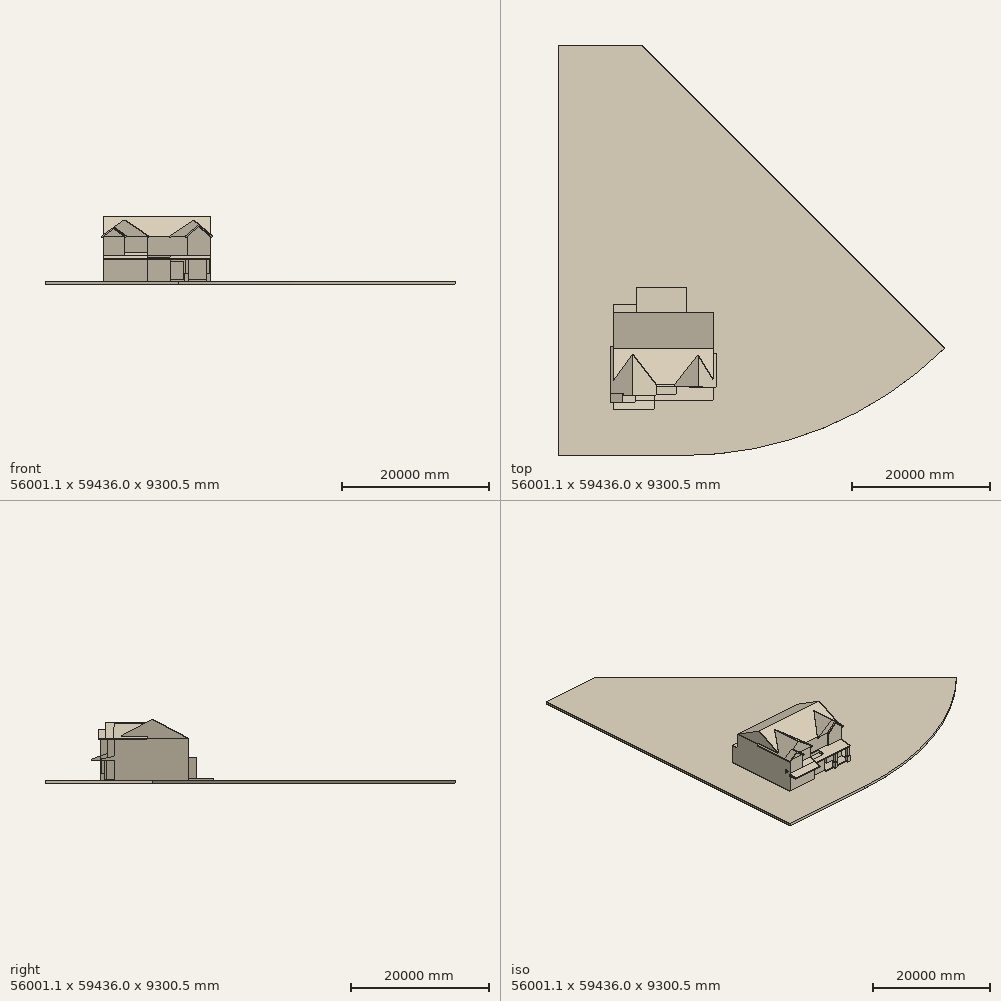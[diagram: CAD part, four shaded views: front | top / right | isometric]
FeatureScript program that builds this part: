
annotation { "Feature Type Name" : "Feature", "Feature Type Description" : "" }
export const myFeature = defineFeature(function(context is Context, id is Id, definition is map)
    precondition{}
    {
        {
            var Q0;
            Q0=qCreatedBy(makeId("Top.planeOp"),FACE);
            var sketch = newSketch(context, id + "F0", { "sketchPlane" : qUnion([Q0])});
            skLineSegment(sketch, "E0", {"start": v(-9470.01, 30042.55) * mm, "end": v(2593.97, 30042.55) * mm});
            skLineSegment(sketch, "E1", {"start": v(8689.97, -29393.45) * mm, "end": v(-9470.01, -29393.45) * mm});
            skLineSegment(sketch, "E2", {"start": v(-9470.01, -29393.45) * mm, "end": v(-9470.01, 30042.55) * mm});
            skLineSegment(sketch, "E3", {"start": v(2593.97, 30042.55) * mm, "end": v(46531.13, -13894.61) * mm});
            skArc(sketch, "E4", {"start": v(8689.97, -29393.45) * mm, "mid": v(29136.04, -25368.6) * mm, "end": v(46531.13, -13894.61) * mm});
            skSolve(sketch);
        }
        {
            var Q0;
            Q0=makeQuery(id+"F0.imprint","IMPRINT",FACE,{"disambiguationData":[TD([[makeQuery(id+"F0.imprint","IMPRINT",EDGE,{"derivedFrom":sQuery(id+"F0.wireOp",EDGE,"E0")}),-1.0]])]});
            extrude(context, id + "F1", {"entities" : qUnion([Q0]), "depth" : 457.2 * mm, "offsetDistance" : 25.4 * mm});
        }
        {
            var Q0;
            Q0=makeQuery(id+"F1.opExtrude","CAP_FACE",FACE,{"disambiguationData":[OSD([sQuery(id+"F0.wireOp",EDGE,"E0"),sQuery(id+"F0.wireOp",EDGE,"E1"),sQuery(id+"F0.wireOp",EDGE,"E2"),sQuery(id+"F0.wireOp",EDGE,"E3"),sQuery(id+"F0.wireOp",EDGE,"E4")])],"isStart":false});
            var sketch = newSketch(context, id + "F2", { "sketchPlane" : qUnion([Q0])});
            skLineSegment(sketch, "E5.bottom", {"start": v(-1545.21, -21468.65) * mm, "end": v(13085.19, -21468.65) * mm});
            skLineSegment(sketch, "E5.top", {"start": v(-1545.21, -8667.05) * mm, "end": v(13085.19, -8667.05) * mm});
            skLineSegment(sketch, "E5.left", {"start": v(-1545.21, -21468.65) * mm, "end": v(-1545.21, -8667.05) * mm});
            skLineSegment(sketch, "E5.right", {"start": v(13085.19, -21468.65) * mm, "end": v(13085.19, -8667.05) * mm});
            skSolve(sketch);
        }
        {
            var Q0;
            Q0 = qSketchRegion(id + "F2", true);
            extrude(context, id + "F3", {"entities" : qUnion([Q0]), "operationType" : NewBodyOperationType.ADD, "depth" : 6096 * mm, "offsetDistance" : 25.4 * mm});
        }
        {
            var Q0;
            Q0=makeQuery(id+"F2.imprint","IMPRINT",FACE,{"disambiguationData":[TD([[makeQuery(id+"F2.imprint","IMPRINT",EDGE,{"derivedFrom":sQuery(id+"F2.wireOp",EDGE,"E5.bottom")}),-1.0]])]});
            var sketch = newSketch(context, id + "F4", { "sketchPlane" : qUnion([Q0])});
            skLineSegment(sketch, "E6.bottom", {"start": v(-1545.21, -7447.85) * mm, "end": v(1807.59, -7447.85) * mm});
            skLineSegment(sketch, "E6.top", {"start": v(-1545.21, -8667.05) * mm, "end": v(1807.59, -8667.05) * mm});
            skLineSegment(sketch, "E6.left", {"start": v(-1545.21, -7447.85) * mm, "end": v(-1545.21, -8667.05) * mm});
            skLineSegment(sketch, "E6.right", {"start": v(1807.59, -7447.85) * mm, "end": v(1807.59, -8667.05) * mm});
            skSolve(sketch);
        }
        {
            var Q0;
            Q0 = qSketchRegion(id + "F4", true);
            extrude(context, id + "F5", {"entities" : qUnion([Q0]), "operationType" : NewBodyOperationType.ADD, "depth" : 3352.8 * mm, "offsetDistance" : 25.4 * mm});
        }
        {
            var Q0;
            Q0=makeQuery(id+"F2.imprint","IMPRINT",FACE,{"disambiguationData":[TD([[makeQuery(id+"F2.imprint","IMPRINT",EDGE,{"derivedFrom":sQuery(id+"F2.wireOp",EDGE,"E5.bottom")}),-1.0]])]});
            var sketch = newSketch(context, id + "F6", { "sketchPlane" : qUnion([Q0])});
            skLineSegment(sketch, "E7.bottom", {"start": v(1807.59, -5009.45) * mm, "end": v(9122.79, -5009.45) * mm});
            skLineSegment(sketch, "E7.top", {"start": v(1807.59, -8667.05) * mm, "end": v(9122.79, -8667.05) * mm});
            skLineSegment(sketch, "E7.left", {"start": v(1807.59, -5009.45) * mm, "end": v(1807.59, -8667.05) * mm});
            skLineSegment(sketch, "E7.right", {"start": v(9122.79, -5009.45) * mm, "end": v(9122.79, -8667.05) * mm});
            skSolve(sketch);
        }
        {
            var Q0;
            Q0 = qSketchRegion(id + "F6", true);
            extrude(context, id + "F7", {"entities" : qUnion([Q0]), "operationType" : NewBodyOperationType.ADD, "depth" : 304.8 * mm, "offsetDistance" : 25.4 * mm});
        }
        {
            var Q0;
            Q0=makeQuery(id+"F3.opExtrude","SWEPT_FACE",FACE,{"disambiguationData":[OSD([sQuery(id+"F2.wireOp",EDGE,"E5.bottom")])]});
            var sketch = newSketch(context, id + "F8", { "sketchPlane" : qUnion([Q0])});
            skLineSegment(sketch, "E8.bottom", {"start": v(13085.19, 457.2) * mm, "end": v(7598.79, 457.2) * mm});
            skLineSegment(sketch, "E8.top", {"start": v(13085.19, 6553.2) * mm, "end": v(7598.79, 6553.2) * mm});
            skLineSegment(sketch, "E8.left", {"start": v(13085.19, 457.2) * mm, "end": v(13085.19, 6553.2) * mm});
            skLineSegment(sketch, "E8.right", {"start": v(7598.79, 457.2) * mm, "end": v(7598.79, 6553.2) * mm});
            skSolve(sketch);
        }
        {
            var Q0;
            Q0 = qSketchRegion(id + "F8", true);
            extrude(context, id + "F9", {"entities" : qUnion([Q0]), "operationType" : NewBodyOperationType.REMOVE, "oppositeDirection" : true, "depth" : 2133.6 * mm, "offsetDistance" : 25.4 * mm});
        }
        {
            var Q0;
            Q0=makeQuery(id+"F3.opExtrude","SWEPT_FACE",FACE,{"disambiguationData":[OSD([sQuery(id+"F2.wireOp",EDGE,"E5.bottom")])]});
            var sketch = newSketch(context, id + "F10", { "sketchPlane" : qUnion([Q0])});
            skLineSegment(sketch, "E9.bottom", {"start": v(7598.79, 6553.2) * mm, "end": v(4398.39, 6553.2) * mm});
            skLineSegment(sketch, "E9.top", {"start": v(7598.79, 457.2) * mm, "end": v(4398.39, 457.2) * mm});
            skLineSegment(sketch, "E9.left", {"start": v(7598.79, 6553.2) * mm, "end": v(7598.79, 457.2) * mm});
            skLineSegment(sketch, "E9.right", {"start": v(4398.39, 6553.2) * mm, "end": v(4398.39, 457.2) * mm});
            skSolve(sketch);
        }
        {
            var Q0;
            Q0 = qSketchRegion(id + "F10", true);
            extrude(context, id + "F11", {"entities" : qUnion([Q0]), "operationType" : NewBodyOperationType.REMOVE, "oppositeDirection" : true, "depth" : 914.4 * mm, "offsetDistance" : 25.4 * mm});
        }
        {
            var Q0;
            Q0=makeQuery(id+"F9.boolean.opBoolean","COPY",FACE,{"derivedFrom":makeQuery(id+"F9.opExtrude","CAP_FACE",FACE,{"disambiguationData":[OSD([sQuery(id+"F8.wireOp",EDGE,"E8.bottom"),sQuery(id+"F8.wireOp",EDGE,"E8.top"),sQuery(id+"F8.wireOp",EDGE,"E8.left"),sQuery(id+"F8.wireOp",EDGE,"E8.right")])],"isStart":false})});
            var sketch = newSketch(context, id + "F12", { "sketchPlane" : qUnion([Q0])});
            skLineSegment(sketch, "E10.bottom", {"start": v(7598.79, 457.2) * mm, "end": v(9427.59, 457.2) * mm});
            skLineSegment(sketch, "E10.top", {"start": v(7598.79, 3200.4) * mm, "end": v(9427.59, 3200.4) * mm});
            skLineSegment(sketch, "E10.left", {"start": v(7598.79, 457.2) * mm, "end": v(7598.79, 3200.4) * mm});
            skLineSegment(sketch, "E10.right", {"start": v(9427.59, 457.2) * mm, "end": v(9427.59, 3200.4) * mm});
            skSolve(sketch);
        }
        {
            var Q0;
            Q0 = qSketchRegion(id + "F12", true);
            extrude(context, id + "F13", {"entities" : qUnion([Q0]), "operationType" : NewBodyOperationType.REMOVE, "oppositeDirection" : true, "depth" : 457.2 * mm, "offsetDistance" : 25.4 * mm});
        }
        {
            var Q0;
            Q0=makeQuery(id+"F3.opExtrude","SWEPT_FACE",FACE,{"disambiguationData":[OSD([sQuery(id+"F2.wireOp",EDGE,"E5.right")])]});
            var sketch = newSketch(context, id + "F14", { "sketchPlane" : qUnion([Q0])});
            skLineSegment(sketch, "E11", {"start": v(-19335.05, 3352.8) * mm, "end": v(-21417.85, 3352.8) * mm});
            skLineSegment(sketch, "E12", {"start": v(-21417.85, 3352.8) * mm, "end": v(-21417.85, 3505.2) * mm});
            skLineSegment(sketch, "E13", {"start": v(-21417.85, 3505.2) * mm, "end": v(-19335.05, 3962.4) * mm});
            skLineSegment(sketch, "E14", {"start": v(-19335.05, 3962.4) * mm, "end": v(-19335.05, 3352.8) * mm});
            skSolve(sketch);
        }
        {
            var Q0;
            Q0 = qSketchRegion(id + "F14", true);
            extrude(context, id + "F15", {"entities" : qUnion([Q0]), "oppositeDirection" : true, "depth" : 8839.2 * mm, "offsetDistance" : 25.4 * mm});
        }
        {
            var Q0;
            Q0=makeQuery(id+"F5.boolean.opBoolean","MERGE",FACE,{"derivedFrom":[makeQuery(id+"F3.opExtrude","SWEPT_FACE",FACE,{"disambiguationData":[OSD([sQuery(id+"F2.wireOp",EDGE,"E5.left")])]}),makeQuery(id+"F5.opExtrude","SWEPT_FACE",FACE,{"disambiguationData":[OSD([sQuery(id+"F4.wireOp",EDGE,"E6.left")])]})]});
            var sketch = newSketch(context, id + "F16", { "sketchPlane" : qUnion([Q0])});
            skLineSegment(sketch, "E15", {"start": v(21468.65, 3352.8) * mm, "end": v(22789.45, 3352.8) * mm});
            skLineSegment(sketch, "E16", {"start": v(22789.45, 3352.8) * mm, "end": v(22789.45, 3505.2) * mm});
            skLineSegment(sketch, "E17", {"start": v(22789.45, 3505.2) * mm, "end": v(21468.65, 3962.4) * mm});
            skLineSegment(sketch, "E18", {"start": v(21468.65, 3962.4) * mm, "end": v(21468.65, 3352.8) * mm});
            skSolve(sketch);
        }
        {
            var Q0;
            Q0 = qSketchRegion(id + "F16", true);
            extrude(context, id + "F17", {"entities" : qUnion([Q0]), "operationType" : NewBodyOperationType.ADD, "oppositeDirection" : true, "depth" : 5943.6 * mm, "offsetDistance" : 25.4 * mm});
        }
        {
            var Q0;
            Q0=makeQuery(id+"F15.opExtrude","SWEPT_FACE",FACE,{"disambiguationData":[OSD([sQuery(id+"F14.wireOp",EDGE,"E11")])]});
            var sketch = newSketch(context, id + "F18", { "sketchPlane" : qUnion([Q0])});
            skLineSegment(sketch, "E19.bottom", {"start": v(13085.19, 21417.85) * mm, "end": v(12475.59, 21417.85) * mm});
            skLineSegment(sketch, "E19.top", {"start": v(13085.19, 20808.25) * mm, "end": v(12475.59, 20808.25) * mm});
            skLineSegment(sketch, "E19.left", {"start": v(13085.19, 21417.85) * mm, "end": v(13085.19, 20808.25) * mm});
            skLineSegment(sketch, "E19.right", {"start": v(12475.59, 21417.85) * mm, "end": v(12475.59, 20808.25) * mm});
            skLineSegment(sketch, "E20.bottom", {"start": v(9511.45, 21417.85) * mm, "end": v(10121.05, 21417.85) * mm});
            skLineSegment(sketch, "E20.top", {"start": v(9511.45, 20808.25) * mm, "end": v(10121.05, 20808.25) * mm});
            skLineSegment(sketch, "E20.left", {"start": v(9511.45, 21417.85) * mm, "end": v(9511.45, 20808.25) * mm});
            skLineSegment(sketch, "E20.right", {"start": v(10121.05, 21417.85) * mm, "end": v(10121.05, 20808.25) * mm});
            skSolve(sketch);
        }
        {
            var Q0;
            Q0 = qSketchRegion(id + "F18", true);
            extrude(context, id + "F19", {"entities" : qUnion([Q0]), "depth" : 3048 * mm, "offsetDistance" : 25.4 * mm});
        }
        {
            var Q0;
            Q0=makeQuery(id+"F13.boolean.opBoolean","MERGE",FACE,{"derivedFrom":[makeQuery(id+"F11.boolean.opBoolean","MERGE",FACE,{"derivedFrom":[makeQuery(id+"F9.boolean.opBoolean","MERGE",FACE,{"derivedFrom":[makeQuery(id+"F1.opExtrude","CAP_FACE",FACE,{"disambiguationData":[OSD([sQuery(id+"F0.wireOp",EDGE,"E0"),sQuery(id+"F0.wireOp",EDGE,"E1"),sQuery(id+"F0.wireOp",EDGE,"E2"),sQuery(id+"F0.wireOp",EDGE,"E3"),sQuery(id+"F0.wireOp",EDGE,"E4")])],"isStart":false})],"fromTools":[makeQuery(id+"F9.opExtrude","SWEPT_FACE",FACE,{"disambiguationData":[OSD([sQuery(id+"F8.wireOp",EDGE,"E8.bottom")])]})]})],"fromTools":[makeQuery(id+"F11.opExtrude","SWEPT_FACE",FACE,{"disambiguationData":[OSD([sQuery(id+"F10.wireOp",EDGE,"E9.top")])]})]})],"fromTools":[makeQuery(id+"F13.opExtrude","SWEPT_FACE",FACE,{"disambiguationData":[OSD([sQuery(id+"F12.wireOp",EDGE,"E10.bottom")])]})]});
            var sketch = newSketch(context, id + "F20", { "sketchPlane" : qUnion([Q0])});
            skLineSegment(sketch, "E21.bottom", {"start": v(7598.79, -18877.85) * mm, "end": v(13078.42, -18877.85) * mm});
            skLineSegment(sketch, "E21.top", {"start": v(7598.79, -21050.32) * mm, "end": v(13078.42, -21050.32) * mm});
            skLineSegment(sketch, "E21.left", {"start": v(7598.79, -18877.85) * mm, "end": v(7598.79, -21050.32) * mm});
            skLineSegment(sketch, "E21.right", {"start": v(13078.42, -18877.85) * mm, "end": v(13078.42, -21050.32) * mm});
            skSolve(sketch);
        }
        {
            var Q0;
            Q0 = qSketchRegion(id + "F20", true);
            extrude(context, id + "F21", {"entities" : qUnion([Q0]), "depth" : 203.2 * mm, "offsetDistance" : 25.4 * mm});
        }
        {
            var Q0;
            Q0=makeQuery(id+"F15.opExtrude","SWEPT_FACE",FACE,{"disambiguationData":[OSD([sQuery(id+"F14.wireOp",EDGE,"E11")])]});
            var sketch = newSketch(context, id + "F22", { "sketchPlane" : qUnion([Q0])});
            skLineSegment(sketch, "E22.bottom", {"start": v(13085.19, 21417.85) * mm, "end": v(12475.59, 21417.85) * mm});
            skLineSegment(sketch, "E22.top", {"start": v(13085.19, 20808.25) * mm, "end": v(12475.59, 20808.25) * mm});
            skLineSegment(sketch, "E22.left", {"start": v(13085.19, 21417.85) * mm, "end": v(13085.19, 20808.25) * mm});
            skLineSegment(sketch, "E22.right", {"start": v(12475.59, 21417.85) * mm, "end": v(12475.59, 20808.25) * mm});
            skLineSegment(sketch, "E23.bottom", {"start": v(10122.32, 21417.85) * mm, "end": v(9487.32, 21417.85) * mm});
            skLineSegment(sketch, "E23.top", {"start": v(10122.32, 20808.25) * mm, "end": v(9487.32, 20808.25) * mm});
            skLineSegment(sketch, "E23.left", {"start": v(10122.32, 21417.85) * mm, "end": v(10122.32, 20808.25) * mm});
            skLineSegment(sketch, "E23.right", {"start": v(9487.32, 21417.85) * mm, "end": v(9487.32, 20808.25) * mm});
            skLineSegment(sketch, "E24.bottom", {"start": v(10020.72, 21316.25) * mm, "end": v(9614.32, 21316.25) * mm});
            skLineSegment(sketch, "E24.top", {"start": v(10020.72, 20909.85) * mm, "end": v(9614.32, 20909.85) * mm});
            skLineSegment(sketch, "E24.left", {"start": v(10020.72, 21316.25) * mm, "end": v(10020.72, 20909.85) * mm});
            skLineSegment(sketch, "E24.right", {"start": v(9614.32, 21316.25) * mm, "end": v(9614.32, 20909.85) * mm});
            skLineSegment(sketch, "E25.bottom", {"start": v(12577.19, 20909.85) * mm, "end": v(12983.59, 20909.85) * mm});
            skLineSegment(sketch, "E25.top", {"start": v(12577.19, 21316.25) * mm, "end": v(12983.59, 21316.25) * mm});
            skLineSegment(sketch, "E25.left", {"start": v(12577.19, 20909.85) * mm, "end": v(12577.19, 21316.25) * mm});
            skLineSegment(sketch, "E25.right", {"start": v(12983.59, 20909.85) * mm, "end": v(12983.59, 21316.25) * mm});
            skSolve(sketch);
        }
        {
            var Q0;
            Q0 = qSketchRegion(id + "F22", true);
            extrude(context, id + "F23", {"entities" : qUnion([Q0]), "operationType" : NewBodyOperationType.REMOVE, "depth" : 1828.8 * mm, "offsetDistance" : 25.4 * mm});
        }
        {
            var Q0;
            Q0=makeQuery(id+"F11.boolean.opBoolean","COPY",FACE,{"derivedFrom":makeQuery(id+"F11.opExtrude","CAP_FACE",FACE,{"disambiguationData":[OSD([sQuery(id+"F10.wireOp",EDGE,"E9.bottom"),sQuery(id+"F10.wireOp",EDGE,"E9.top"),sQuery(id+"F10.wireOp",EDGE,"E9.left"),sQuery(id+"F10.wireOp",EDGE,"E9.right")])],"isStart":false})});
            var sketch = newSketch(context, id + "F24", { "sketchPlane" : qUnion([Q0])});
            skLineSegment(sketch, "E26.bottom", {"start": v(4398.39, 6553.2) * mm, "end": v(7598.79, 6553.2) * mm});
            skLineSegment(sketch, "E26.top", {"start": v(4398.39, 3505.2) * mm, "end": v(7598.79, 3505.2) * mm});
            skLineSegment(sketch, "E26.left", {"start": v(4398.39, 6553.2) * mm, "end": v(4398.39, 3505.2) * mm});
            skLineSegment(sketch, "E26.right", {"start": v(7598.79, 6553.2) * mm, "end": v(7598.79, 3505.2) * mm});
            skSolve(sketch);
        }
        {
            var Q0;
            Q0 = qSketchRegion(id + "F24", true);
            extrude(context, id + "F25", {"entities" : qUnion([Q0]), "operationType" : NewBodyOperationType.REMOVE, "oppositeDirection" : true, "depth" : 1219.2 * mm, "offsetDistance" : 25.4 * mm});
        }
        {
            var Q0;
            Q0=makeQuery(id+"F25.boolean.opBoolean","MERGE",FACE,{"derivedFrom":[makeQuery(id+"F9.boolean.opBoolean","COPY",FACE,{"derivedFrom":makeQuery(id+"F9.opExtrude","CAP_FACE",FACE,{"disambiguationData":[OSD([sQuery(id+"F8.wireOp",EDGE,"E8.bottom"),sQuery(id+"F8.wireOp",EDGE,"E8.top"),sQuery(id+"F8.wireOp",EDGE,"E8.left"),sQuery(id+"F8.wireOp",EDGE,"E8.right")])],"isStart":false})})],"fromTools":[makeQuery(id+"F25.opExtrude","CAP_FACE",FACE,{"disambiguationData":[OSD([sQuery(id+"F24.wireOp",EDGE,"E26.bottom"),sQuery(id+"F24.wireOp",EDGE,"E26.top"),sQuery(id+"F24.wireOp",EDGE,"E26.left"),sQuery(id+"F24.wireOp",EDGE,"E26.right")])],"isStart":false})]});
            var sketch = newSketch(context, id + "F26", { "sketchPlane" : qUnion([Q0])});
            skLineSegment(sketch, "E27.bottom", {"start": v(4398.39, 6553.2) * mm, "end": v(9914.34, 6553.2) * mm});
            skLineSegment(sketch, "E27.top", {"start": v(4398.39, 3962.4) * mm, "end": v(9914.34, 3962.4) * mm});
            skLineSegment(sketch, "E27.left", {"start": v(4398.39, 6553.2) * mm, "end": v(4398.39, 3962.4) * mm});
            skLineSegment(sketch, "E27.right", {"start": v(9914.34, 6553.2) * mm, "end": v(9914.34, 3962.4) * mm});
            skSolve(sketch);
        }
        {
            var Q0;
            Q0 = qSketchRegion(id + "F26", true);
            extrude(context, id + "F27", {"entities" : qUnion([Q0]), "operationType" : NewBodyOperationType.REMOVE, "oppositeDirection" : true, "depth" : 254 * mm, "offsetDistance" : 25.4 * mm});
        }
        {
            var Q0;
            {var subQ1=sQuery(id+"F2.wireOp",EDGE,"E5.bottom");var subQ2=sQuery(id+"F16.wireOp",EDGE,"E17");Q0=makeQuery(id+"F17.boolean.opBoolean","SPLIT",FACE,{"disambiguationData":[TD([makeQuery(id+"F17.opExtrude","SWEPT_FACE",FACE,{"disambiguationData":[OSD([subQ2])]})])],"derivedFrom":makeQuery(id+"F3.opExtrude","SWEPT_FACE",FACE,{"disambiguationData":[OSD([subQ1])]})});}
            var sketch = newSketch(context, id + "F28", { "sketchPlane" : qUnion([Q0])});
            skLineSegment(sketch, "E28.bottom", {"start": v(4398.39, 6553.2) * mm, "end": v(1350.39, 6553.2) * mm});
            skLineSegment(sketch, "E28.top", {"start": v(4398.39, 3962.4) * mm, "end": v(1350.39, 3962.4) * mm});
            skLineSegment(sketch, "E28.left", {"start": v(4398.39, 6553.2) * mm, "end": v(4398.39, 3962.4) * mm});
            skLineSegment(sketch, "E28.right", {"start": v(1350.39, 6553.2) * mm, "end": v(1350.39, 3962.4) * mm});
            skSolve(sketch);
        }
        {
            var Q0;
            Q0 = qSketchRegion(id + "F28", true);
            extrude(context, id + "F29", {"entities" : qUnion([Q0]), "operationType" : NewBodyOperationType.REMOVE, "oppositeDirection" : true, "depth" : 1066.8 * mm, "offsetDistance" : 25.4 * mm});
        }
        {
            var Q0;
            {var subQ3=sQuery(id+"F16.wireOp",EDGE,"E18");Q0=makeQuery(id+"F16.imprint","IMPRINT",FACE,{"disambiguationData":[TD([[makeQuery(id+"F16.imprint","IMPRINT",EDGE,{"derivedFrom":subQ3}),-1.0]])]});}
            var sketch = newSketch(context, id + "F30", { "sketchPlane" : qUnion([Q0])});
            skLineSegment(sketch, "E29", {"start": v(21468.65, 3962.4) * mm, "end": v(21468.65, 3352.8) * mm});
            skLineSegment(sketch, "E30", {"start": v(21468.65, 3962.4) * mm, "end": v(20342.53, 4352.21) * mm});
            skLineSegment(sketch, "E31", {"start": v(20342.53, 4352.21) * mm, "end": v(20342.53, 3352.8) * mm});
            skLineSegment(sketch, "E32", {"start": v(20342.53, 3352.8) * mm, "end": v(21468.65, 3352.8) * mm});
            skSolve(sketch);
        }
        {
            var Q0;
            Q0 = qSketchRegion(id + "F30", true);
            extrude(context, id + "F31", {"entities" : qUnion([Q0]), "oppositeDirection" : true, "depth" : 5943.6 * mm, "offsetDistance" : 25.4 * mm});
        }
        {
            var Q0;
            {var subQ3=sQuery(id+"F14.wireOp",EDGE,"E14");Q0=makeQuery(id+"F14.imprint","IMPRINT",FACE,{"disambiguationData":[TD([[makeQuery(id+"F14.imprint","IMPRINT",EDGE,{"derivedFrom":subQ3}),1.0]])]});}
            var sketch = newSketch(context, id + "F32", { "sketchPlane" : qUnion([Q0])});
            skLineSegment(sketch, "E33", {"start": v(-19335.05, 3962.4) * mm, "end": v(-19335.05, 3352.8) * mm});
            skLineSegment(sketch, "E34", {"start": v(-19335.05, 3962.4) * mm, "end": v(-18821.67, 4075.1) * mm});
            skLineSegment(sketch, "E35", {"start": v(-18821.67, 4075.1) * mm, "end": v(-18821.67, 3352.8) * mm});
            skLineSegment(sketch, "E36", {"start": v(-18821.67, 3352.8) * mm, "end": v(-19335.05, 3352.8) * mm});
            skSolve(sketch);
        }
        {
            var Q0;
            Q0 = qSketchRegion(id + "F32", true);
            extrude(context, id + "F33", {"entities" : qUnion([Q0]), "operationType" : NewBodyOperationType.ADD, "oppositeDirection" : true, "depth" : 9144 * mm, "offsetDistance" : 25.4 * mm});
        }
        {
            var Q0;
            Q0=makeQuery(id+"F29.boolean.opBoolean","COPY",FACE,{"derivedFrom":makeQuery(id+"F29.opExtrude","CAP_FACE",FACE,{"disambiguationData":[OSD([sQuery(id+"F28.wireOp",EDGE,"E28.bottom"),sQuery(id+"F28.wireOp",EDGE,"E28.top"),sQuery(id+"F28.wireOp",EDGE,"E28.left"),sQuery(id+"F28.wireOp",EDGE,"E28.right")])],"isStart":false})});
            var sketch = newSketch(context, id + "F34", { "sketchPlane" : qUnion([Q0])});
            skLineSegment(sketch, "E37", {"start": v(1655.19, 6553.2) * mm, "end": v(-1850.01, 6553.2) * mm});
            skLineSegment(sketch, "E38", {"start": v(-1850.01, 6553.2) * mm, "end": v(-97.41, 7823.2) * mm});
            skLineSegment(sketch, "E39", {"start": v(-97.41, 7823.2) * mm, "end": v(1655.19, 6553.2) * mm});
            skLineSegment(sketch, "E40.bottom", {"start": v(1655.19, 6553.2) * mm, "end": v(1350.39, 6553.2) * mm});
            skLineSegment(sketch, "E40.top", {"start": v(1655.19, 6400.8) * mm, "end": v(1350.39, 6400.8) * mm});
            skLineSegment(sketch, "E40.left", {"start": v(1655.19, 6553.2) * mm, "end": v(1655.19, 6400.8) * mm});
            skLineSegment(sketch, "E40.right", {"start": v(1350.39, 6553.2) * mm, "end": v(1350.39, 6400.8) * mm});
            skLineSegment(sketch, "E41.bottom", {"start": v(-1850.01, 6553.2) * mm, "end": v(-1545.21, 6553.2) * mm});
            skLineSegment(sketch, "E41.top", {"start": v(-1850.01, 6400.8) * mm, "end": v(-1545.21, 6400.8) * mm});
            skLineSegment(sketch, "E41.left", {"start": v(-1850.01, 6553.2) * mm, "end": v(-1850.01, 6400.8) * mm});
            skLineSegment(sketch, "E41.right", {"start": v(-1545.21, 6553.2) * mm, "end": v(-1545.21, 6400.8) * mm});
            skSolve(sketch);
        }
        {
            var Q0;
            Q0 = qSketchRegion(id + "F34", true);
            var Q1;
            {var subQ1=sQuery(id+"F2.wireOp",EDGE,"E5.bottom");var subQ2=sQuery(id+"F16.wireOp",EDGE,"E17");Q1=makeQuery(id+"F17.boolean.opBoolean","SPLIT",FACE,{"disambiguationData":[TD([makeQuery(id+"F17.opExtrude","SWEPT_FACE",FACE,{"disambiguationData":[OSD([subQ2])]})])],"derivedFrom":makeQuery(id+"F3.opExtrude","SWEPT_FACE",FACE,{"disambiguationData":[OSD([subQ1])]})});}
            extrude(context, id + "F35", {"entities" : qUnion([Q0]), "depth" : 1295.4 * mm, "endBoundEntityFace" : qUnion([Q1]), "offsetDistance" : 25.4 * mm});
        }
        {
            var Q0;
            Q0=makeQuery(id+"F35.opExtrude","CAP_FACE",FACE,{"disambiguationData":[OSD([sQuery(id+"F34.wireOp",EDGE,"E37"),sQuery(id+"F34.wireOp",EDGE,"E38"),sQuery(id+"F34.wireOp",EDGE,"E39"),sQuery(id+"F34.wireOp",EDGE,"E40.top"),sQuery(id+"F34.wireOp",EDGE,"E40.left"),sQuery(id+"F34.wireOp",EDGE,"E40.right"),sQuery(id+"F34.wireOp",EDGE,"E41.top"),sQuery(id+"F34.wireOp",EDGE,"E41.left"),sQuery(id+"F34.wireOp",EDGE,"E41.right")])],"isStart":true});
            var sketch = newSketch(context, id + "F36", { "sketchPlane" : qUnion([Q0])});
            skLineSegment(sketch, "E42", {"start": v(1545.21, 6400.8) * mm, "end": v(1850.01, 6400.8) * mm});
            skLineSegment(sketch, "E43", {"start": v(1850.01, 6400.8) * mm, "end": v(1850.01, 6553.2) * mm});
            skLineSegment(sketch, "E44", {"start": v(1850.01, 6553.2) * mm, "end": v(-1314.77, 8846.52) * mm});
            skLineSegment(sketch, "E45", {"start": v(-1314.77, 8846.52) * mm, "end": v(-4703.19, 6553.2) * mm});
            skLineSegment(sketch, "E46", {"start": v(1545.21, 6553.2) * mm, "end": v(1545.21, 6400.8) * mm});
            skLineSegment(sketch, "E47.top", {"start": v(-4703.19, 6400.8) * mm, "end": v(-4398.39, 6400.8) * mm});
            skLineSegment(sketch, "E47.left", {"start": v(-4703.19, 6553.2) * mm, "end": v(-4703.19, 6400.8) * mm});
            skLineSegment(sketch, "E47.right", {"start": v(-4398.39, 6553.2) * mm, "end": v(-4398.39, 6400.8) * mm});
            skLineSegment(sketch, "E48", {"start": v(-4398.39, 6553.2) * mm, "end": v(1545.21, 6553.2) * mm});
            skSolve(sketch);
        }
        {
            var Q0;
            Q0 = qSketchRegion(id + "F36", true);
            extrude(context, id + "F37", {"entities" : qUnion([Q0]), "depth" : 6756.4 * mm, "offsetDistance" : 25.4 * mm, "hasSecondDirection" : true, "secondDirectionOppositeDirection" : true, "secondDirectionDepth" : 254 * mm});
        }
        {
            var Q0;
            Q0=makeQuery(id+"F27.boolean.opBoolean","COPY",FACE,{"derivedFrom":makeQuery(id+"F27.opExtrude","CAP_FACE",FACE,{"disambiguationData":[OSD([sQuery(id+"F26.wireOp",EDGE,"E27.bottom"),sQuery(id+"F26.wireOp",EDGE,"E27.top"),sQuery(id+"F26.wireOp",EDGE,"E27.left"),sQuery(id+"F26.wireOp",EDGE,"E27.right")])],"isStart":false})});
            var sketch = newSketch(context, id + "F38", { "sketchPlane" : qUnion([Q0])});
            skLineSegment(sketch, "E49.top", {"start": v(9914.34, 6400.8) * mm, "end": v(9609.54, 6400.8) * mm});
            skLineSegment(sketch, "E49.left", {"start": v(9914.34, 6553.2) * mm, "end": v(9914.34, 6400.8) * mm});
            skLineSegment(sketch, "E49.right", {"start": v(9609.54, 6553.2) * mm, "end": v(9609.54, 6400.8) * mm});
            skLineSegment(sketch, "E50", {"start": v(9609.54, 6553.2) * mm, "end": v(11499.77, 8171.52) * mm});
            skLineSegment(sketch, "E51", {"start": v(11499.77, 8171.52) * mm, "end": v(13389.99, 6553.2) * mm});
            skLineSegment(sketch, "E52.top", {"start": v(13389.99, 6400.8) * mm, "end": v(13085.19, 6400.8) * mm});
            skLineSegment(sketch, "E52.left", {"start": v(13389.99, 6553.2) * mm, "end": v(13389.99, 6400.8) * mm});
            skLineSegment(sketch, "E52.right", {"start": v(13085.19, 6553.2) * mm, "end": v(13085.19, 6400.8) * mm});
            skLineSegment(sketch, "E53", {"start": v(9914.34, 6553.2) * mm, "end": v(13085.19, 6553.2) * mm});
            skLineSegment(sketch, "E54", {"start": v(9914.34, 6553.2) * mm, "end": v(9609.54, 6553.2) * mm});
            skLineSegment(sketch, "E55", {"start": v(13389.99, 6553.2) * mm, "end": v(13085.19, 6553.2) * mm});
            skSolve(sketch);
        }
        {
            var Q0;
            Q0=makeQuery(id+"F38.imprint","IMPRINT",FACE,{"disambiguationData":[TD([[makeQuery(id+"F38.imprint","IMPRINT",EDGE,{"derivedFrom":sQuery(id+"F38.wireOp",EDGE,"E49.top")}),-1.0]])]});
            var Q1;
            Q1=makeQuery(id+"F38.imprint","IMPRINT",FACE,{"disambiguationData":[TD([[makeQuery(id+"F38.imprint","IMPRINT",EDGE,{"derivedFrom":sQuery(id+"F38.wireOp",EDGE,"E50")}),-1.0]])]});
            var Q2;
            Q2=makeQuery(id+"F38.imprint","IMPRINT",FACE,{"disambiguationData":[TD([[makeQuery(id+"F38.imprint","IMPRINT",EDGE,{"derivedFrom":sQuery(id+"F38.wireOp",EDGE,"E52.top")}),-1.0]])]});
            extrude(context, id + "F39", {"entities" : qUnion([Q0, Q1, Q2]), "operationType" : NewBodyOperationType.ADD, "depth" : 508 * mm, "offsetDistance" : 25.4 * mm});
        }
        {
            var Q0;
            Q0=makeQuery(id+"F39.opExtrude","CAP_FACE",FACE,{"disambiguationData":[OSD([sQuery(id+"F38.wireOp",EDGE,"E49.top"),sQuery(id+"F38.wireOp",EDGE,"E49.left"),sQuery(id+"F38.wireOp",EDGE,"E49.right"),sQuery(id+"F38.wireOp",EDGE,"E50"),sQuery(id+"F38.wireOp",EDGE,"E51"),sQuery(id+"F38.wireOp",EDGE,"E52.top"),sQuery(id+"F38.wireOp",EDGE,"E52.left"),sQuery(id+"F38.wireOp",EDGE,"E52.right"),sQuery(id+"F38.wireOp",EDGE,"E53")])],"isStart":true});
            var sketch = newSketch(context, id + "F40", { "sketchPlane" : qUnion([Q0])});
            skLineSegment(sketch, "E56", {"start": v(-13085.19, 6553.2) * mm, "end": v(-13085.19, 6400.8) * mm});
            skLineSegment(sketch, "E57", {"start": v(-13085.19, 6400.8) * mm, "end": v(-13389.99, 6400.8) * mm});
            skLineSegment(sketch, "E58", {"start": v(-13389.99, 6400.8) * mm, "end": v(-13389.99, 6553.2) * mm});
            skLineSegment(sketch, "E59", {"start": v(-13389.99, 6553.2) * mm, "end": v(-10788.61, 8780.37) * mm});
            skLineSegment(sketch, "E60", {"start": v(-10788.61, 8780.37) * mm, "end": v(-7433.16, 6553.2) * mm});
            skLineSegment(sketch, "E61", {"start": v(-7433.16, 6553.2) * mm, "end": v(-13085.19, 6553.2) * mm});
            skLineSegment(sketch, "E62.bottom", {"start": v(-7433.16, 6553.2) * mm, "end": v(-7737.96, 6553.2) * mm});
            skLineSegment(sketch, "E62.top", {"start": v(-7433.16, 6400.8) * mm, "end": v(-7737.96, 6400.8) * mm});
            skLineSegment(sketch, "E62.left", {"start": v(-7433.16, 6553.2) * mm, "end": v(-7433.16, 6400.8) * mm});
            skLineSegment(sketch, "E62.right", {"start": v(-7737.96, 6553.2) * mm, "end": v(-7737.96, 6400.8) * mm});
            skSolve(sketch);
        }
        {
            var Q0;
            Q0 = qSketchRegion(id + "F40", true);
            extrude(context, id + "F41", {"entities" : qUnion([Q0]), "operationType" : NewBodyOperationType.ADD, "depth" : 4419.6 * mm, "offsetDistance" : 25.4 * mm, "hasSecondDirection" : true, "secondDirectionOppositeDirection" : true, "secondDirectionDepth" : 254 * mm});
        }
        {
            var Q0;
            {var subQ3=sQuery(id+"F14.wireOp",EDGE,"E14");Q0=makeQuery(id+"F14.imprint","IMPRINT",FACE,{"disambiguationData":[TD([[makeQuery(id+"F14.imprint","IMPRINT",EDGE,{"derivedFrom":subQ3}),1.0]])]});}
            var sketch = newSketch(context, id + "F42", { "sketchPlane" : qUnion([Q0])});
            skLineSegment(sketch, "E63", {"start": v(-8667.05, 6553.2) * mm, "end": v(-13874.05, 9300.54) * mm});
            skLineSegment(sketch, "E64", {"start": v(-13874.05, 9300.54) * mm, "end": v(-19081.05, 6553.2) * mm});
            skLineSegment(sketch, "E65", {"start": v(-19081.05, 6553.2) * mm, "end": v(-8667.05, 6553.2) * mm});
            skSolve(sketch);
        }
        {
            var Q0;
            Q0=makeQuery(id+"F42.imprint","IMPRINT",FACE,{"disambiguationData":[TD([[makeQuery(id+"F42.imprint","IMPRINT",EDGE,{"derivedFrom":sQuery(id+"F42.wireOp",EDGE,"E63")}),1.0]])]});
            extrude(context, id + "F43", {"entities" : qUnion([Q0]), "oppositeDirection" : true, "depth" : 14630.4 * mm, "offsetDistance" : 25.4 * mm});
        }
        {
            var Q0;
            Q0=makeQuery(id+"F35.opExtrude","CAP_FACE",FACE,{"disambiguationData":[OSD([sQuery(id+"F34.wireOp",EDGE,"E37"),sQuery(id+"F34.wireOp",EDGE,"E38"),sQuery(id+"F34.wireOp",EDGE,"E39"),sQuery(id+"F34.wireOp",EDGE,"E40.top"),sQuery(id+"F34.wireOp",EDGE,"E40.left"),sQuery(id+"F34.wireOp",EDGE,"E40.right"),sQuery(id+"F34.wireOp",EDGE,"E41.top"),sQuery(id+"F34.wireOp",EDGE,"E41.left"),sQuery(id+"F34.wireOp",EDGE,"E41.right")])],"isStart":false});
            var sketch = newSketch(context, id + "F44", { "sketchPlane" : qUnion([Q0])});
            skLineSegment(sketch, "E66", {"start": v(-1545.21, 6553.2) * mm, "end": v(-97.41, 7602.33) * mm});
            skLineSegment(sketch, "E67", {"start": v(-97.41, 7602.33) * mm, "end": v(1350.39, 6553.2) * mm});
            skLineSegment(sketch, "E68", {"start": v(1350.39, 6553.2) * mm, "end": v(-1545.21, 6553.2) * mm});
            skSolve(sketch);
        }
        {
            var Q0;
            Q0=makeQuery(id+"F44.imprint","IMPRINT",FACE,{"disambiguationData":[TD([[makeQuery(id+"F44.imprint","IMPRINT",EDGE,{"derivedFrom":sQuery(id+"F44.wireOp",EDGE,"E66")}),-1.0]])]});
            extrude(context, id + "F45", {"entities" : qUnion([Q0]), "operationType" : NewBodyOperationType.REMOVE, "oppositeDirection" : true, "depth" : 228.6 * mm, "offsetDistance" : 25.4 * mm});
        }
        {
            var Q0;
            Q0=makeQuery(id+"F39.opExtrude","CAP_FACE",FACE,{"disambiguationData":[OSD([sQuery(id+"F38.wireOp",EDGE,"E49.top"),sQuery(id+"F38.wireOp",EDGE,"E49.left"),sQuery(id+"F38.wireOp",EDGE,"E49.right"),sQuery(id+"F38.wireOp",EDGE,"E50"),sQuery(id+"F38.wireOp",EDGE,"E51"),sQuery(id+"F38.wireOp",EDGE,"E52.top"),sQuery(id+"F38.wireOp",EDGE,"E52.left"),sQuery(id+"F38.wireOp",EDGE,"E52.right"),sQuery(id+"F38.wireOp",EDGE,"E53")])],"isStart":false});
            var sketch = newSketch(context, id + "F46", { "sketchPlane" : qUnion([Q0])});
            skLineSegment(sketch, "E69", {"start": v(9914.34, 6553.2) * mm, "end": v(11499.77, 7910.56) * mm});
            skLineSegment(sketch, "E70", {"start": v(11499.77, 7910.56) * mm, "end": v(13085.19, 6553.2) * mm});
            skLineSegment(sketch, "E71", {"start": v(13085.19, 6553.2) * mm, "end": v(9914.34, 6553.2) * mm});
            skSolve(sketch);
        }
        {
            var Q0;
            Q0=makeQuery(id+"F46.imprint","IMPRINT",FACE,{"disambiguationData":[TD([[makeQuery(id+"F46.imprint","IMPRINT",EDGE,{"derivedFrom":sQuery(id+"F46.wireOp",EDGE,"E69")}),-1.0]])]});
            extrude(context, id + "F47", {"entities" : qUnion([Q0]), "operationType" : NewBodyOperationType.REMOVE, "oppositeDirection" : true, "depth" : 254 * mm, "offsetDistance" : 25.4 * mm});
        }
    });
